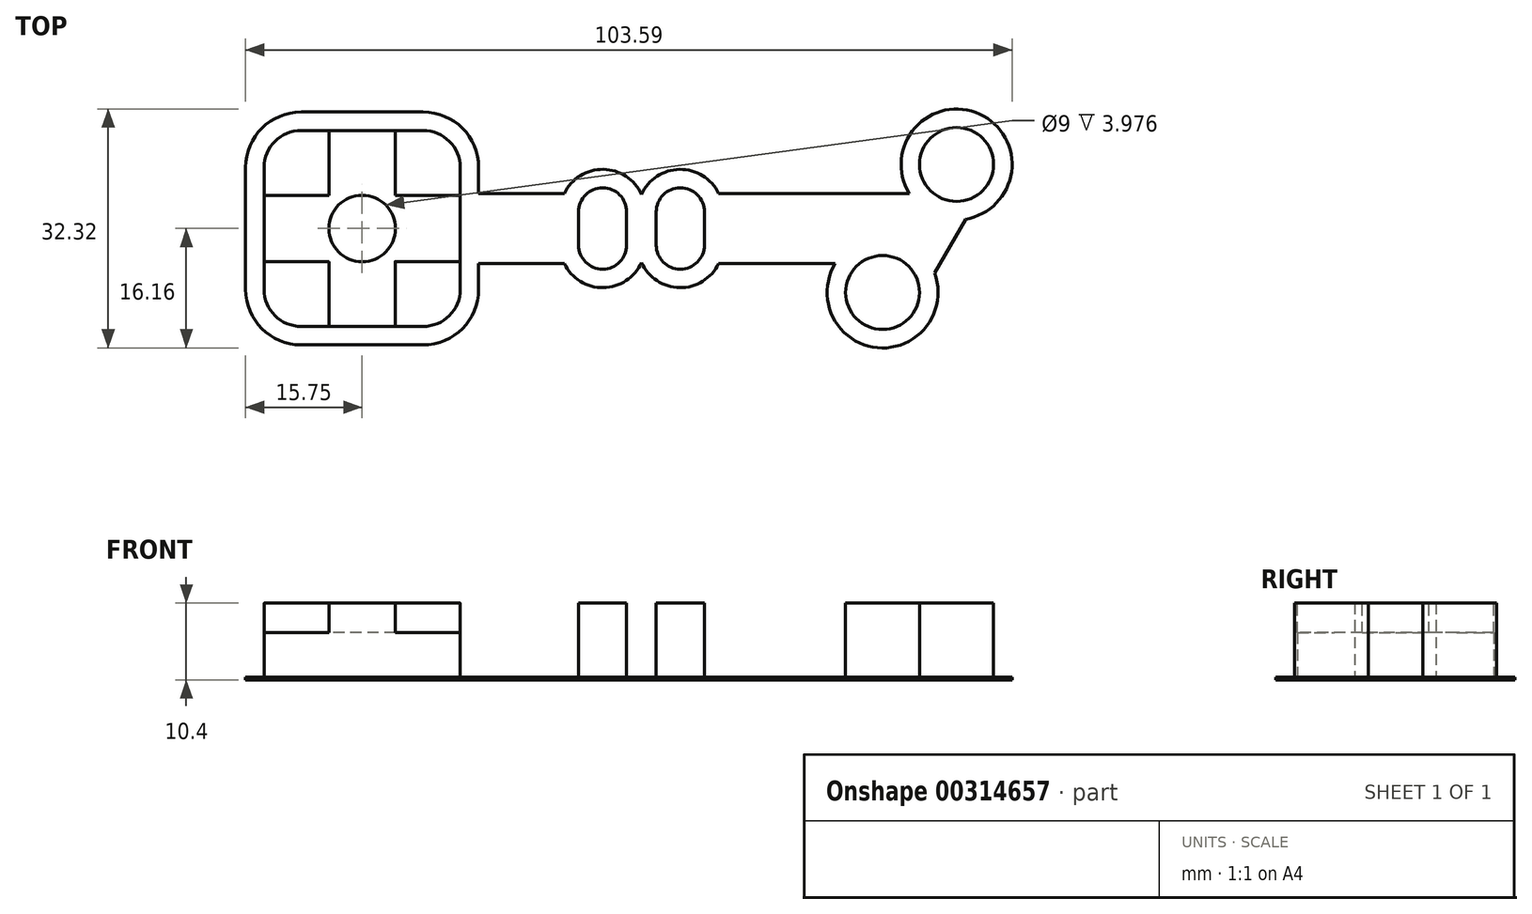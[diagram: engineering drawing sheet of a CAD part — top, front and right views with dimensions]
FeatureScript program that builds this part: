
annotation { "Feature Type Name" : "Feature", "Feature Type Description" : "" }
export const myFeature = defineFeature(function(context is Context, id is Id, definition is map)
    precondition{}
    {
        {
            var Q0;
            Q0=qCreatedBy(makeId("Top.planeOp"),FACE);
            var sketch = newSketch(context, id + "F0", { "sketchPlane" : qUnion([Q0])});
            skLineSegment(sketch, "E0.bottom", {"start": v(-8.25, 13.25) * mm, "end": v(8.25, 13.25) * mm});
            skLineSegment(sketch, "E0.top", {"start": v(-8.25, -13.25) * mm, "end": v(8.25, -13.25) * mm});
            skLineSegment(sketch, "E0.left", {"start": v(-13.25, 8.25) * mm, "end": v(-13.25, -8.25) * mm});
            skLineSegment(sketch, "E0.right", {"start": v(13.25, 8.25) * mm, "end": v(13.25, 2.25) * mm});
            skPoint(sketch, "E0.middle", {"position": v(0, 0) * mm});
            skPoint(sketch, "E1.visualSharp", {"position": v(-13.25, 13.25) * mm});
            skArc(sketch, "E1.filletArc", {"start": v(-8.25, 13.25) * mm, "mid": v(-11.79, 11.79) * mm, "end": v(-13.25, 8.25) * mm});
            skPoint(sketch, "E2.visualSharp", {"position": v(13.25, 13.25) * mm});
            skArc(sketch, "E2.filletArc", {"start": v(13.25, 8.25) * mm, "mid": v(11.79, 11.79) * mm, "end": v(8.25, 13.25) * mm});
            skPoint(sketch, "E3.visualSharp", {"position": v(13.25, -13.25) * mm});
            skArc(sketch, "E3.filletArc", {"start": v(8.25, -13.25) * mm, "mid": v(11.79, -11.79) * mm, "end": v(13.25, -8.25) * mm});
            skPoint(sketch, "E4.visualSharp", {"position": v(-13.25, -13.25) * mm});
            skArc(sketch, "E4.filletArc", {"start": v(-13.25, -8.25) * mm, "mid": v(-11.79, -11.79) * mm, "end": v(-8.25, -13.25) * mm});
            skCircle(sketch, "E5", {"center": v(0, 0) * mm, "radius": 4.5 * mm});
            skLineSegment(sketch, "E6", {"start": v(-93.44, 0) * mm, "end": v(130.36, 0) * mm, "construction": true});
            skPoint(sketch, "E6.startSnap0", {"position": v(-13.25, 0) * mm});
            skLineSegment(sketch, "E7", {"start": v(-4.5, 13.25) * mm, "end": v(-4.5, -13.25) * mm});
            skLineSegment(sketch, "E8", {"start": v(4.5, 13.25) * mm, "end": v(4.5, -13.25) * mm});
            skLineSegment(sketch, "E9", {"start": v(-13.25, -4.5) * mm, "end": v(13.25, -4.5) * mm});
            skLineSegment(sketch, "E10", {"start": v(-13.25, 4.5) * mm, "end": v(13.25, 4.5) * mm});
            skLineSegment(sketch, "E11", {"start": v(13.25, 2.25) * mm, "end": v(13.25, 2.25) * mm});
            skLineSegment(sketch, "E12.bottom", {"start": v(29.25, 2.25) * mm, "end": v(35.75, 2.25) * mm});
            skLineSegment(sketch, "E12.top", {"start": v(29.25, -2.25) * mm, "end": v(35.75, -2.25) * mm});
            skLineSegment(sketch, "E12.left", {"start": v(29.25, 2.25) * mm, "end": v(29.25, -2.25) * mm});
            skLineSegment(sketch, "E12.right", {"start": v(35.75, 2.25) * mm, "end": v(35.75, -2.25) * mm});
            skLineSegment(sketch, "E13", {"start": v(37.75, 15.2) * mm, "end": v(37.75, -16.91) * mm, "construction": true});
            skLineSegment(sketch, "E14.MirrorCS", {"start": v(13.25, -2.25) * mm, "end": v(29.25, -2.25) * mm});
            skLineSegment(sketch, "E15.MirrorCS", {"start": v(39.75, 2.25) * mm, "end": v(39.75, -2.25) * mm});
            skLineSegment(sketch, "E16.MirrorCS", {"start": v(46.25, -2.25) * mm, "end": v(39.75, -2.25) * mm});
            skLineSegment(sketch, "E17.MirrorCS", {"start": v(46.25, 2.25) * mm, "end": v(46.25, -2.25) * mm});
            skLineSegment(sketch, "E18.MirrorCS", {"start": v(46.25, 2.25) * mm, "end": v(39.75, 2.25) * mm});
            skLineSegment(sketch, "E19", {"start": v(35.75, 2.25) * mm, "end": v(39.75, 2.25) * mm});
            skLineSegment(sketch, "E20", {"start": v(39.75, -2.25) * mm, "end": v(35.75, -2.25) * mm});
            skArc(sketch, "E21", {"start": v(35.75, 2.25) * mm, "mid": v(32.5, 5.5) * mm, "end": v(29.25, 2.25) * mm});
            skArc(sketch, "E22", {"start": v(35.75, -2.25) * mm, "mid": v(32.5, -5.5) * mm, "end": v(29.25, -2.25) * mm});
            skArc(sketch, "E23.MirrorCS", {"start": v(39.75, 2.25) * mm, "mid": v(43, 5.5) * mm, "end": v(46.25, 2.25) * mm});
            skArc(sketch, "E24.MirrorCS", {"start": v(39.75, -2.25) * mm, "mid": v(43, -5.5) * mm, "end": v(46.25, -2.25) * mm});
            skLineSegment(sketch, "E25", {"start": v(46.25, 2.25) * mm, "end": v(74.04, 2.25) * mm});
            skLineSegment(sketch, "E26", {"start": v(80.34, 8.66) * mm, "end": v(70.34, -8.66) * mm, "construction": true});
            skPoint(sketch, "E27", {"position": v(75.34, 0) * mm});
            skLineSegment(sketch, "E28", {"start": v(76.16, 5.92) * mm, "end": v(74.04, 2.25) * mm});
            skPoint(sketch, "E29", {"position": v(73.39, 1.12) * mm});
            skLineSegment(sketch, "E30.MirrorCS", {"start": v(80.05, 3.67) * mm, "end": v(80.05, 3.67) * mm});
            skLineSegment(sketch, "E31.MirrorCS", {"start": v(46.25, -2.25) * mm, "end": v(71.44, -2.25) * mm});
            skPoint(sketch, "E32", {"position": v(72.74, 0) * mm});
            skPoint(sketch, "E33.orphan", {"position": v(72.75, -2.25) * mm});
            skPoint(sketch, "E34.orphan", {"position": v(72.75, 2.25) * mm});
            skLineSegment(sketch, "E35", {"start": v(13.25, 2.25) * mm, "end": v(29.25, 2.25) * mm});
            skLineSegment(sketch, "E36", {"start": v(13.25, -2.25) * mm, "end": v(13.25, -8.25) * mm});
            skLineSegment(sketch, "E37", {"start": v(13.25, 2.25) * mm, "end": v(13.25, -2.25) * mm});
            skLineSegment(sketch, "E38", {"start": v(71.44, -2.25) * mm, "end": v(70.62, -3.67) * mm});
            skLineSegment(sketch, "E39", {"start": v(74.04, 2.25) * mm, "end": v(71.44, -2.25) * mm});
            skArc(sketch, "E40", {"start": v(70.62, -3.67) * mm, "mid": v(67.84, -13) * mm, "end": v(74.52, -5.92) * mm});
            skArc(sketch, "E41", {"start": v(74.52, -5.92) * mm, "mid": v(72.84, -4.33) * mm, "end": v(70.62, -3.67) * mm});
            skLineSegment(sketch, "E42", {"start": v(80.05, 3.67) * mm, "end": v(74.52, -5.92) * mm});
            skArc(sketch, "E43", {"start": v(76.16, 5.92) * mm, "mid": v(77.84, 4.33) * mm, "end": v(80.05, 3.67) * mm});
            skArc(sketch, "E44", {"start": v(80.05, 3.67) * mm, "mid": v(82.84, 13) * mm, "end": v(76.16, 5.92) * mm});
            skLineSegment(sketch, "E45.0", {"start": v(-8.25, 15.75) * mm, "end": v(8.25, 15.75) * mm});
            skArc(sketch, "E45.1", {"start": v(15.75, 8.25) * mm, "mid": v(13.55, 13.55) * mm, "end": v(8.25, 15.75) * mm});
            skLineSegment(sketch, "E45.2", {"start": v(15.75, 8.25) * mm, "end": v(15.75, 4.75) * mm});
            skLineSegment(sketch, "E45.3", {"start": v(15.75, 4.75) * mm, "end": v(27.32, 4.75) * mm});
            skArc(sketch, "E45.4", {"start": v(37.75, 4.6) * mm, "mid": v(32.59, 8) * mm, "end": v(27.32, 4.75) * mm});
            skArc(sketch, "E45.5", {"start": v(-8.25, 15.75) * mm, "mid": v(-13.55, 13.55) * mm, "end": v(-15.75, 8.25) * mm});
            skArc(sketch, "E45.6", {"start": v(37.75, 4.6) * mm, "mid": v(42.91, 8) * mm, "end": v(48.18, 4.75) * mm});
            skLineSegment(sketch, "E45.7", {"start": v(48.18, 4.75) * mm, "end": v(73.94, 4.75) * mm});
            skArc(sketch, "E45.8", {"start": v(81.55, 1.26) * mm, "mid": v(83.46, 15.48) * mm, "end": v(73.94, 4.75) * mm});
            skLineSegment(sketch, "E45.9", {"start": v(81.55, 1.26) * mm, "end": v(77.35, -6) * mm});
            skArc(sketch, "E45.10", {"start": v(8.25, -15.75) * mm, "mid": v(13.55, -13.55) * mm, "end": v(15.75, -8.25) * mm});
            skLineSegment(sketch, "E45.11", {"start": v(-8.25, -15.75) * mm, "end": v(8.25, -15.75) * mm});
            skArc(sketch, "E45.12", {"start": v(-15.75, -8.25) * mm, "mid": v(-13.55, -13.55) * mm, "end": v(-8.25, -15.75) * mm});
            skLineSegment(sketch, "E45.13", {"start": v(-15.75, 8.25) * mm, "end": v(-15.75, -8.25) * mm});
            skLineSegment(sketch, "E45.14", {"start": v(15.75, -4.75) * mm, "end": v(15.75, -8.25) * mm});
            skLineSegment(sketch, "E45.15", {"start": v(15.75, -4.75) * mm, "end": v(27.32, -4.75) * mm});
            skArc(sketch, "E45.16", {"start": v(37.75, -4.6) * mm, "mid": v(32.59, -8) * mm, "end": v(27.32, -4.75) * mm});
            skArc(sketch, "E45.17", {"start": v(37.75, -4.6) * mm, "mid": v(42.91, -8) * mm, "end": v(48.18, -4.75) * mm});
            skLineSegment(sketch, "E45.18", {"start": v(48.18, -4.75) * mm, "end": v(63.94, -4.75) * mm});
            skArc(sketch, "E45.19", {"start": v(63.94, -4.75) * mm, "mid": v(69.64, -16.13) * mm, "end": v(77.35, -6) * mm});
            skSolve(sketch);
        }
        {
            var Q0;
            {var subQ15=sQuery(id+"F0.wireOp",EDGE,"E1.filletArc");Q0=makeQuery(id+"F0.imprint","IMPRINT",FACE,{"disambiguationData":[TD([[makeQuery(id+"F0.imprint","IMPRINT",EDGE,{"derivedFrom":subQ15}),-1.0]])]});}
            var Q1;
            {var subQ2=sQuery(id+"F0.wireOp",EDGE,"E7");var subQ5=sQuery(id+"F0.wireOp",EDGE,"E0.top");var subQ8=makeQuery(id+"F0.imprint","INTERSECT",VERTEX,{"derivedFrom":[subQ5,subQ2]});Q1=makeQuery(id+"F0.imprint","IMPRINT",FACE,{"disambiguationData":[TD([[makeQuery(id+"F0.imprint","IMPRINT",EDGE,{"disambiguationData":[TD([[subQ8,-1.0]])],"derivedFrom":subQ5}),1.0]])]});}
            var Q2;
            Q2=makeQuery(id+"F0.imprint","IMPRINT",FACE,{"disambiguationData":[TD([[makeQuery(id+"F0.imprint","IMPRINT",EDGE,{"derivedFrom":sQuery(id+"F0.wireOp",EDGE,"E28")}),1.0]])]});
            var Q3;
            Q3=makeQuery(id+"F0.imprint","IMPRINT",FACE,{"disambiguationData":[TD([[makeQuery(id+"F0.imprint","IMPRINT",EDGE,{"derivedFrom":sQuery(id+"F0.wireOp",EDGE,"E12.bottom")}),-1.0]])]});
            var Q4;
            Q4=makeQuery(id+"F0.imprint","IMPRINT",FACE,{"disambiguationData":[TD([[makeQuery(id+"F0.imprint","IMPRINT",EDGE,{"derivedFrom":sQuery(id+"F0.wireOp",EDGE,"E12.bottom")}),1.0]])]});
            var Q5;
            Q5=makeQuery(id+"F0.imprint","IMPRINT",FACE,{"disambiguationData":[TD([[makeQuery(id+"F0.imprint","IMPRINT",EDGE,{"derivedFrom":sQuery(id+"F0.wireOp",EDGE,"E17.MirrorCS")}),1.0]])]});
            var Q6;
            Q6=makeQuery(id+"F0.imprint","IMPRINT",FACE,{"disambiguationData":[TD([[makeQuery(id+"F0.imprint","IMPRINT",EDGE,{"derivedFrom":sQuery(id+"F0.wireOp",EDGE,"E12.top")}),-1.0]])]});
            var Q7;
            Q7=makeQuery(id+"F0.imprint","IMPRINT",FACE,{"disambiguationData":[TD([[makeQuery(id+"F0.imprint","IMPRINT",EDGE,{"derivedFrom":sQuery(id+"F0.wireOp",EDGE,"E12.right")}),1.0]])]});
            var Q8;
            {var subQ2=sQuery(id+"F0.wireOp",EDGE,"E9");var subQ6=sQuery(id+"F0.wireOp",EDGE,"E0.left");var subQ8=makeQuery(id+"F0.imprint","INTERSECT",VERTEX,{"derivedFrom":[subQ6,subQ2]});Q8=makeQuery(id+"F0.imprint","IMPRINT",FACE,{"disambiguationData":[TD([[makeQuery(id+"F0.imprint","IMPRINT",EDGE,{"disambiguationData":[TD([[subQ8,1.0]])],"derivedFrom":subQ6}),1.0]])]});}
            var Q9;
            Q9=makeQuery(id+"F0.imprint","IMPRINT",FACE,{"disambiguationData":[TD([[makeQuery(id+"F0.imprint","IMPRINT",EDGE,{"derivedFrom":sQuery(id+"F0.wireOp",EDGE,"E18.MirrorCS")}),-1.0]])]});
            var Q10;
            {var subQ5=sQuery(id+"F0.wireOp",EDGE,"E4.filletArc");Q10=makeQuery(id+"F0.imprint","IMPRINT",FACE,{"disambiguationData":[TD([[makeQuery(id+"F0.imprint","IMPRINT",EDGE,{"derivedFrom":subQ5}),1.0]])]});}
            var Q11;
            {var subQ5=sQuery(id+"F0.wireOp",EDGE,"E3.filletArc");Q11=makeQuery(id+"F0.imprint","IMPRINT",FACE,{"disambiguationData":[TD([[makeQuery(id+"F0.imprint","IMPRINT",EDGE,{"derivedFrom":subQ5}),1.0]])]});}
            var Q12;
            Q12=makeQuery(id+"F0.imprint","IMPRINT",FACE,{"disambiguationData":[TD([[makeQuery(id+"F0.imprint","IMPRINT",EDGE,{"derivedFrom":sQuery(id+"F0.wireOp",EDGE,"E16.MirrorCS")}),1.0]])]});
            var Q13;
            Q13=makeQuery(id+"F0.imprint","IMPRINT",FACE,{"disambiguationData":[TD([[makeQuery(id+"F0.imprint","IMPRINT",EDGE,{"derivedFrom":sQuery(id+"F0.wireOp",EDGE,"E40")}),1.0]])]});
            var Q14;
            Q14=makeQuery(id+"F0.imprint","IMPRINT",FACE,{"disambiguationData":[TD([[makeQuery(id+"F0.imprint","IMPRINT",EDGE,{"derivedFrom":sQuery(id+"F0.wireOp",EDGE,"E43")}),1.0]])]});
            var Q15;
            {var subQ8=sQuery(id+"F0.wireOp",EDGE,"E37");Q15=makeQuery(id+"F0.imprint","IMPRINT",FACE,{"disambiguationData":[TD([[makeQuery(id+"F0.imprint","IMPRINT",EDGE,{"derivedFrom":subQ8}),-1.0]])]});}
            var Q16;
            {var subQ5=sQuery(id+"F0.wireOp",EDGE,"E1.filletArc");Q16=makeQuery(id+"F0.imprint","IMPRINT",FACE,{"disambiguationData":[TD([[makeQuery(id+"F0.imprint","IMPRINT",EDGE,{"derivedFrom":subQ5}),1.0]])]});}
            var Q17;
            {var subQ2=sQuery(id+"F0.wireOp",EDGE,"E7");var subQ5=sQuery(id+"F0.wireOp",EDGE,"E0.bottom");var subQ8=makeQuery(id+"F0.imprint","INTERSECT",VERTEX,{"derivedFrom":[subQ5,subQ2]});Q17=makeQuery(id+"F0.imprint","IMPRINT",FACE,{"disambiguationData":[TD([[makeQuery(id+"F0.imprint","IMPRINT",EDGE,{"disambiguationData":[TD([[subQ8,-1.0]])],"derivedFrom":subQ5}),-1.0]])]});}
            var Q18;
            {var subQ5=sQuery(id+"F0.wireOp",EDGE,"E2.filletArc");Q18=makeQuery(id+"F0.imprint","IMPRINT",FACE,{"disambiguationData":[TD([[makeQuery(id+"F0.imprint","IMPRINT",EDGE,{"derivedFrom":subQ5}),1.0]])]});}
            var Q19;
            Q19=makeQuery(id+"F0.imprint","IMPRINT",FACE,{"disambiguationData":[TD([[makeQuery(id+"F0.imprint","IMPRINT",EDGE,{"derivedFrom":sQuery(id+"F0.wireOp",EDGE,"E12.left")}),-1.0]])]});
            var Q20;
            Q20=makeQuery(id+"F0.imprint","IMPRINT",FACE,{"disambiguationData":[TD([[makeQuery(id+"F0.imprint","IMPRINT",EDGE,{"derivedFrom":sQuery(id+"F0.wireOp",EDGE,"E15.MirrorCS")}),1.0]])]});
            var Q21;
            {var subQ0=sQuery(id+"F0.wireOp",EDGE,"E5");var subQ1=makeQuery(id+"F0.imprint","INTERSECT",VERTEX,{"derivedFrom":[subQ0,sQuery(id+"F0.wireOp",EDGE,"E10")]});Q21=makeQuery(id+"F0.imprint","IMPRINT",FACE,{"disambiguationData":[TD([[makeQuery(id+"F0.imprint","IMPRINT",EDGE,{"disambiguationData":[TD([[subQ1,1.0]])],"derivedFrom":subQ0}),1.0]])]});}
            var Q22;
            {var subQ0=sQuery(id+"F0.wireOp",EDGE,"E10");var subQ1=sQuery(id+"F0.wireOp",EDGE,"E5");var subQ2=makeQuery(id+"F0.imprint","INTERSECT",VERTEX,{"derivedFrom":[subQ1,subQ0]});Q22=makeQuery(id+"F0.imprint","IMPRINT",FACE,{"disambiguationData":[TD([[makeQuery(id+"F0.imprint","IMPRINT",EDGE,{"disambiguationData":[TD([[subQ2,1.0]])],"derivedFrom":subQ1}),-1.0]])]});}
            var Q23;
            {var subQ0=sQuery(id+"F0.wireOp",EDGE,"E8");var subQ1=sQuery(id+"F0.wireOp",EDGE,"E5");var subQ2=makeQuery(id+"F0.imprint","INTERSECT",VERTEX,{"derivedFrom":[subQ1,subQ0]});Q23=makeQuery(id+"F0.imprint","IMPRINT",FACE,{"disambiguationData":[TD([[makeQuery(id+"F0.imprint","IMPRINT",EDGE,{"disambiguationData":[TD([[subQ2,1.0]])],"derivedFrom":subQ1}),-1.0]])]});}
            var Q24;
            {var subQ0=sQuery(id+"F0.wireOp",EDGE,"E7");var subQ1=sQuery(id+"F0.wireOp",EDGE,"E5");var subQ2=makeQuery(id+"F0.imprint","INTERSECT",VERTEX,{"derivedFrom":[subQ1,subQ0]});Q24=makeQuery(id+"F0.imprint","IMPRINT",FACE,{"disambiguationData":[TD([[makeQuery(id+"F0.imprint","IMPRINT",EDGE,{"disambiguationData":[TD([[subQ2,-1.0]])],"derivedFrom":subQ1}),-1.0]])]});}
            var Q25;
            {var subQ0=sQuery(id+"F0.wireOp",EDGE,"E10");var subQ1=sQuery(id+"F0.wireOp",EDGE,"E5");var subQ2=makeQuery(id+"F0.imprint","INTERSECT",VERTEX,{"derivedFrom":[subQ1,subQ0]});Q25=makeQuery(id+"F0.imprint","IMPRINT",FACE,{"disambiguationData":[TD([[makeQuery(id+"F0.imprint","IMPRINT",EDGE,{"disambiguationData":[TD([[subQ2,-1.0]])],"derivedFrom":subQ1}),-1.0]])]});}
            extrude(context, id + "F1", {"entities" : qUnion([Q0, Q1, Q2, Q3, Q4, Q5, Q6, Q7, Q8, Q9, Q10, Q11, Q12, Q13, Q14, Q15, Q16, Q17, Q18, Q19, Q20, Q21, Q22, Q23, Q24, Q25]), "depth" : 0.4 * mm});
        }
        {
            var Q0;
            Q0=makeQuery(id+"F1.opExtrude","CAP_FACE",FACE,{"disambiguationData":[OSD([sQuery(id+"F0.wireOp",EDGE,"E45.0"),sQuery(id+"F0.wireOp",EDGE,"E45.1"),sQuery(id+"F0.wireOp",EDGE,"E45.2"),sQuery(id+"F0.wireOp",EDGE,"E45.3"),sQuery(id+"F0.wireOp",EDGE,"E45.4"),sQuery(id+"F0.wireOp",EDGE,"E45.5"),sQuery(id+"F0.wireOp",EDGE,"E45.6"),sQuery(id+"F0.wireOp",EDGE,"E45.7"),sQuery(id+"F0.wireOp",EDGE,"E45.8"),sQuery(id+"F0.wireOp",EDGE,"E45.9"),sQuery(id+"F0.wireOp",EDGE,"E45.10"),sQuery(id+"F0.wireOp",EDGE,"E45.11"),sQuery(id+"F0.wireOp",EDGE,"E45.12"),sQuery(id+"F0.wireOp",EDGE,"E45.13"),sQuery(id+"F0.wireOp",EDGE,"E45.14"),sQuery(id+"F0.wireOp",EDGE,"E45.15"),sQuery(id+"F0.wireOp",EDGE,"E45.16"),sQuery(id+"F0.wireOp",EDGE,"E45.17"),sQuery(id+"F0.wireOp",EDGE,"E45.18"),sQuery(id+"F0.wireOp",EDGE,"E45.19")])],"isStart":false});
            var sketch = newSketch(context, id + "F2", { "sketchPlane" : qUnion([Q0])});
            skLineSegment(sketch, "E46.0", {"start": v(-8.25, 13.25) * mm, "end": v(8.25, 13.25) * mm});
            skLineSegment(sketch, "E46.1", {"start": v(-8.25, -13.25) * mm, "end": v(8.25, -13.25) * mm});
            skLineSegment(sketch, "E46.2", {"start": v(-13.25, 8.25) * mm, "end": v(-13.25, -8.25) * mm});
            skLineSegment(sketch, "E46.3", {"start": v(13.25, 8.25) * mm, "end": v(13.25, 2.25) * mm});
            skPoint(sketch, "E46.4", {"position": v(0, 0) * mm});
            skPoint(sketch, "E46.5", {"position": v(-13.25, 13.25) * mm});
            skArc(sketch, "E46.6", {"start": v(-8.25, 13.25) * mm, "mid": v(-11.79, 11.79) * mm, "end": v(-13.25, 8.25) * mm});
            skPoint(sketch, "E46.7", {"position": v(13.25, 13.25) * mm});
            skArc(sketch, "E46.8", {"start": v(13.25, 8.25) * mm, "mid": v(11.79, 11.79) * mm, "end": v(8.25, 13.25) * mm});
            skPoint(sketch, "E46.9", {"position": v(13.25, -13.25) * mm});
            skArc(sketch, "E46.10", {"start": v(8.25, -13.25) * mm, "mid": v(11.79, -11.79) * mm, "end": v(13.25, -8.25) * mm});
            skPoint(sketch, "E46.11", {"position": v(-13.25, -13.25) * mm});
            skArc(sketch, "E46.12", {"start": v(-13.25, -8.25) * mm, "mid": v(-11.79, -11.79) * mm, "end": v(-8.25, -13.25) * mm});
            skCircle(sketch, "E46.13", {"center": v(0, 0) * mm, "radius": 4.5 * mm});
            skPoint(sketch, "E46.15", {"position": v(-13.25, 0) * mm});
            skLineSegment(sketch, "E46.16", {"start": v(-4.5, 13.25) * mm, "end": v(-4.5, -13.25) * mm});
            skLineSegment(sketch, "E46.17", {"start": v(4.5, 13.25) * mm, "end": v(4.5, -13.25) * mm});
            skLineSegment(sketch, "E46.18", {"start": v(-13.25, -4.5) * mm, "end": v(13.25, -4.5) * mm});
            skLineSegment(sketch, "E46.19", {"start": v(-13.25, 4.5) * mm, "end": v(13.25, 4.5) * mm});
            skPoint(sketch, "E46.20", {"position": v(13.25, 2.25) * mm});
            skLineSegment(sketch, "E46.21", {"start": v(29.25, 2.25) * mm, "end": v(35.75, 2.25) * mm});
            skLineSegment(sketch, "E46.22", {"start": v(29.25, -2.25) * mm, "end": v(35.75, -2.25) * mm});
            skLineSegment(sketch, "E46.23", {"start": v(29.25, 2.25) * mm, "end": v(29.25, -2.25) * mm});
            skLineSegment(sketch, "E46.24", {"start": v(35.75, 2.25) * mm, "end": v(35.75, -2.25) * mm});
            skLineSegment(sketch, "E46.26", {"start": v(13.25, -2.25) * mm, "end": v(29.25, -2.25) * mm});
            skLineSegment(sketch, "E46.27", {"start": v(39.75, 2.25) * mm, "end": v(39.75, -2.25) * mm});
            skLineSegment(sketch, "E46.28", {"start": v(46.25, -2.25) * mm, "end": v(39.75, -2.25) * mm});
            skLineSegment(sketch, "E46.29", {"start": v(46.25, 2.25) * mm, "end": v(46.25, -2.25) * mm});
            skLineSegment(sketch, "E46.30", {"start": v(46.25, 2.25) * mm, "end": v(39.75, 2.25) * mm});
            skLineSegment(sketch, "E46.31", {"start": v(35.75, 2.25) * mm, "end": v(39.75, 2.25) * mm});
            skLineSegment(sketch, "E46.32", {"start": v(39.75, -2.25) * mm, "end": v(35.75, -2.25) * mm});
            skArc(sketch, "E46.33", {"start": v(35.75, 2.25) * mm, "mid": v(32.5, 5.5) * mm, "end": v(29.25, 2.25) * mm});
            skArc(sketch, "E46.34", {"start": v(35.75, -2.25) * mm, "mid": v(32.5, -5.5) * mm, "end": v(29.25, -2.25) * mm});
            skArc(sketch, "E46.35", {"start": v(39.75, 2.25) * mm, "mid": v(43, 5.5) * mm, "end": v(46.25, 2.25) * mm});
            skArc(sketch, "E46.36", {"start": v(35.75, 2.25) * mm, "mid": v(32.5, 5.5) * mm, "end": v(29.25, 2.25) * mm});
            skArc(sketch, "E46.37", {"start": v(39.75, -2.25) * mm, "mid": v(43, -5.5) * mm, "end": v(46.25, -2.25) * mm});
            skLineSegment(sketch, "E46.38", {"start": v(46.25, 2.25) * mm, "end": v(74.04, 2.25) * mm});
            skLineSegment(sketch, "E46.39", {"start": v(80.34, 8.66) * mm, "end": v(70.34, -8.66) * mm});
            skPoint(sketch, "E46.40", {"position": v(75.34, 0) * mm});
            skLineSegment(sketch, "E46.41", {"start": v(76.16, 5.92) * mm, "end": v(74.04, 2.25) * mm});
            skPoint(sketch, "E46.42", {"position": v(73.39, 1.12) * mm});
            skPoint(sketch, "E46.43", {"position": v(80.05, 3.67) * mm});
            skLineSegment(sketch, "E46.44", {"start": v(46.25, -2.25) * mm, "end": v(71.44, -2.25) * mm});
            skPoint(sketch, "E46.45", {"position": v(72.74, 0) * mm});
            skPoint(sketch, "E46.46", {"position": v(72.75, -2.25) * mm});
            skPoint(sketch, "E46.47", {"position": v(72.75, 2.25) * mm});
            skLineSegment(sketch, "E46.48", {"start": v(13.25, 2.25) * mm, "end": v(29.25, 2.25) * mm});
            skLineSegment(sketch, "E46.49", {"start": v(13.25, -2.25) * mm, "end": v(13.25, -8.25) * mm});
            skLineSegment(sketch, "E46.50", {"start": v(13.25, 2.25) * mm, "end": v(13.25, -2.25) * mm});
            skLineSegment(sketch, "E46.51", {"start": v(71.44, -2.25) * mm, "end": v(70.62, -3.67) * mm});
            skLineSegment(sketch, "E46.52", {"start": v(74.04, 2.25) * mm, "end": v(71.44, -2.25) * mm});
            skArc(sketch, "E46.53", {"start": v(70.62, -3.67) * mm, "mid": v(67.84, -13) * mm, "end": v(74.52, -5.92) * mm});
            skArc(sketch, "E46.54", {"start": v(74.52, -5.92) * mm, "mid": v(72.84, -4.33) * mm, "end": v(70.62, -3.67) * mm});
            skLineSegment(sketch, "E46.55", {"start": v(80.05, 3.67) * mm, "end": v(74.52, -5.92) * mm});
            skArc(sketch, "E46.56", {"start": v(76.16, 5.92) * mm, "mid": v(77.84, 4.33) * mm, "end": v(80.05, 3.67) * mm});
            skArc(sketch, "E46.57", {"start": v(80.05, 3.67) * mm, "mid": v(82.84, 13) * mm, "end": v(76.16, 5.92) * mm});
            skLineSegment(sketch, "E46.58", {"start": v(-8.25, 15.75) * mm, "end": v(8.25, 15.75) * mm});
            skArc(sketch, "E46.59", {"start": v(15.75, 8.25) * mm, "mid": v(13.55, 13.55) * mm, "end": v(8.25, 15.75) * mm});
            skLineSegment(sketch, "E46.60", {"start": v(15.75, 8.25) * mm, "end": v(15.75, 4.75) * mm});
            skLineSegment(sketch, "E46.61", {"start": v(15.75, 4.75) * mm, "end": v(27.32, 4.75) * mm});
            skArc(sketch, "E46.62", {"start": v(37.75, 4.6) * mm, "mid": v(32.59, 8) * mm, "end": v(27.32, 4.75) * mm});
            skArc(sketch, "E46.63", {"start": v(-8.25, 15.75) * mm, "mid": v(-13.55, 13.55) * mm, "end": v(-15.75, 8.25) * mm});
            skArc(sketch, "E46.64", {"start": v(37.75, 4.6) * mm, "mid": v(42.91, 8) * mm, "end": v(48.18, 4.75) * mm});
            skLineSegment(sketch, "E46.65", {"start": v(48.18, 4.75) * mm, "end": v(73.94, 4.75) * mm});
            skArc(sketch, "E46.66", {"start": v(81.55, 1.26) * mm, "mid": v(83.46, 15.48) * mm, "end": v(73.94, 4.75) * mm});
            skLineSegment(sketch, "E46.67", {"start": v(81.55, 1.26) * mm, "end": v(77.35, -6) * mm});
            skArc(sketch, "E46.68", {"start": v(8.25, -15.75) * mm, "mid": v(13.55, -13.55) * mm, "end": v(15.75, -8.25) * mm});
            skLineSegment(sketch, "E46.69", {"start": v(-8.25, -15.75) * mm, "end": v(8.25, -15.75) * mm});
            skArc(sketch, "E46.70", {"start": v(-15.75, -8.25) * mm, "mid": v(-13.55, -13.55) * mm, "end": v(-8.25, -15.75) * mm});
            skLineSegment(sketch, "E46.71", {"start": v(-15.75, 8.25) * mm, "end": v(-15.75, -8.25) * mm});
            skLineSegment(sketch, "E46.72", {"start": v(15.75, -4.75) * mm, "end": v(15.75, -8.25) * mm});
            skLineSegment(sketch, "E46.73", {"start": v(15.75, -4.75) * mm, "end": v(27.32, -4.75) * mm});
            skArc(sketch, "E46.74", {"start": v(37.75, -4.6) * mm, "mid": v(32.59, -8) * mm, "end": v(27.32, -4.75) * mm});
            skArc(sketch, "E46.75", {"start": v(37.75, -4.6) * mm, "mid": v(42.91, -8) * mm, "end": v(48.18, -4.75) * mm});
            skLineSegment(sketch, "E46.76", {"start": v(48.18, -4.75) * mm, "end": v(63.94, -4.75) * mm});
            skArc(sketch, "E46.77", {"start": v(63.94, -4.75) * mm, "mid": v(69.64, -16.13) * mm, "end": v(77.35, -6) * mm});
            skSolve(sketch);
        }
        {
            var Q0;
            {var subQ2=sQuery(id+"F2.wireOp",EDGE,"E46.16");var subQ5=sQuery(id+"F2.wireOp",EDGE,"E46.0");var subQ8=makeQuery(id+"F2.imprint","INTERSECT",VERTEX,{"derivedFrom":[subQ5,subQ2]});Q0=makeQuery(id+"F2.imprint","IMPRINT",FACE,{"disambiguationData":[TD([[makeQuery(id+"F2.imprint","IMPRINT",EDGE,{"disambiguationData":[TD([[subQ8,-1.0]])],"derivedFrom":subQ5}),-1.0]])]});}
            var Q1;
            {var subQ2=sQuery(id+"F2.wireOp",EDGE,"E46.18");var subQ6=sQuery(id+"F2.wireOp",EDGE,"E46.2");var subQ8=makeQuery(id+"F2.imprint","INTERSECT",VERTEX,{"derivedFrom":[subQ6,subQ2]});Q1=makeQuery(id+"F2.imprint","IMPRINT",FACE,{"disambiguationData":[TD([[makeQuery(id+"F2.imprint","IMPRINT",EDGE,{"disambiguationData":[TD([[subQ8,1.0]])],"derivedFrom":subQ6}),1.0]])]});}
            var Q2;
            {var subQ4=sQuery(id+"F2.wireOp",EDGE,"E46.50");Q2=makeQuery(id+"F2.imprint","IMPRINT",FACE,{"disambiguationData":[TD([[makeQuery(id+"F2.imprint","IMPRINT",EDGE,{"derivedFrom":subQ4}),-1.0]])]});}
            var Q3;
            {var subQ2=sQuery(id+"F2.wireOp",EDGE,"E46.16");var subQ5=sQuery(id+"F2.wireOp",EDGE,"E46.1");var subQ8=makeQuery(id+"F2.imprint","INTERSECT",VERTEX,{"derivedFrom":[subQ5,subQ2]});Q3=makeQuery(id+"F2.imprint","IMPRINT",FACE,{"disambiguationData":[TD([[makeQuery(id+"F2.imprint","IMPRINT",EDGE,{"disambiguationData":[TD([[subQ8,-1.0]])],"derivedFrom":subQ5}),1.0]])]});}
            var Q4;
            {var subQ0=sQuery(id+"F2.wireOp",EDGE,"E46.17");var subQ1=sQuery(id+"F2.wireOp",EDGE,"E46.13");var subQ2=makeQuery(id+"F2.imprint","INTERSECT",VERTEX,{"derivedFrom":[subQ1,subQ0]});Q4=makeQuery(id+"F2.imprint","IMPRINT",FACE,{"disambiguationData":[TD([[makeQuery(id+"F2.imprint","IMPRINT",EDGE,{"disambiguationData":[TD([[subQ2,1.0]])],"derivedFrom":subQ1}),-1.0]])]});}
            var Q5;
            {var subQ0=sQuery(id+"F2.wireOp",EDGE,"E46.16");var subQ1=sQuery(id+"F2.wireOp",EDGE,"E46.13");var subQ2=makeQuery(id+"F2.imprint","INTERSECT",VERTEX,{"derivedFrom":[subQ1,subQ0]});Q5=makeQuery(id+"F2.imprint","IMPRINT",FACE,{"disambiguationData":[TD([[makeQuery(id+"F2.imprint","IMPRINT",EDGE,{"disambiguationData":[TD([[subQ2,-1.0]])],"derivedFrom":subQ1}),-1.0]])]});}
            var Q6;
            {var subQ0=sQuery(id+"F2.wireOp",EDGE,"E46.19");var subQ1=sQuery(id+"F2.wireOp",EDGE,"E46.13");var subQ2=makeQuery(id+"F2.imprint","INTERSECT",VERTEX,{"derivedFrom":[subQ1,subQ0]});Q6=makeQuery(id+"F2.imprint","IMPRINT",FACE,{"disambiguationData":[TD([[makeQuery(id+"F2.imprint","IMPRINT",EDGE,{"disambiguationData":[TD([[subQ2,-1.0]])],"derivedFrom":subQ1}),-1.0]])]});}
            var Q7;
            {var subQ0=sQuery(id+"F2.wireOp",EDGE,"E46.19");var subQ1=sQuery(id+"F2.wireOp",EDGE,"E46.13");var subQ2=makeQuery(id+"F2.imprint","INTERSECT",VERTEX,{"derivedFrom":[subQ1,subQ0]});Q7=makeQuery(id+"F2.imprint","IMPRINT",FACE,{"disambiguationData":[TD([[makeQuery(id+"F2.imprint","IMPRINT",EDGE,{"disambiguationData":[TD([[subQ2,1.0]])],"derivedFrom":subQ1}),-1.0]])]});}
            var Q8;
            Q8=makeQuery(id+"F2.imprint","IMPRINT",FACE,{"disambiguationData":[TD([[makeQuery(id+"F2.imprint","IMPRINT",EDGE,{"derivedFrom":sQuery(id+"F2.wireOp",EDGE,"E46.21")}),-1.0]])]});
            var Q9;
            Q9=makeQuery(id+"F2.imprint","IMPRINT",FACE,{"disambiguationData":[TD([[makeQuery(id+"F2.imprint","IMPRINT",EDGE,{"derivedFrom":sQuery(id+"F2.wireOp",EDGE,"E46.21")}),1.0]])]});
            var Q10;
            Q10=makeQuery(id+"F2.imprint","IMPRINT",FACE,{"disambiguationData":[TD([[makeQuery(id+"F2.imprint","IMPRINT",EDGE,{"derivedFrom":sQuery(id+"F2.wireOp",EDGE,"E46.22")}),-1.0]])]});
            var Q11;
            Q11=makeQuery(id+"F2.imprint","IMPRINT",FACE,{"disambiguationData":[TD([[makeQuery(id+"F2.imprint","IMPRINT",EDGE,{"derivedFrom":sQuery(id+"F2.wireOp",EDGE,"E46.30")}),-1.0]])]});
            var Q12;
            Q12=makeQuery(id+"F2.imprint","IMPRINT",FACE,{"disambiguationData":[TD([[makeQuery(id+"F2.imprint","IMPRINT",EDGE,{"derivedFrom":sQuery(id+"F2.wireOp",EDGE,"E46.27")}),1.0]])]});
            var Q13;
            Q13=makeQuery(id+"F2.imprint","IMPRINT",FACE,{"disambiguationData":[TD([[makeQuery(id+"F2.imprint","IMPRINT",EDGE,{"derivedFrom":sQuery(id+"F2.wireOp",EDGE,"E46.28")}),1.0]])]});
            var Q14;
            {var subQ0=sQuery(id+"F2.wireOp",EDGE,"E46.57");Q14=makeQuery(id+"F2.imprint","IMPRINT",FACE,{"disambiguationData":[TD([[makeQuery(id+"F2.imprint","IMPRINT",EDGE,{"derivedFrom":subQ0}),1.0]])]});}
            var Q15;
            {var subQ0=sQuery(id+"F2.wireOp",EDGE,"E46.53");Q15=makeQuery(id+"F2.imprint","IMPRINT",FACE,{"disambiguationData":[TD([[makeQuery(id+"F2.imprint","IMPRINT",EDGE,{"derivedFrom":subQ0}),1.0]])]});}
            var Q16;
            {var subQ5=sQuery(id+"F2.wireOp",EDGE,"E46.8");Q16=makeQuery(id+"F2.imprint","IMPRINT",FACE,{"disambiguationData":[TD([[makeQuery(id+"F2.imprint","IMPRINT",EDGE,{"derivedFrom":subQ5}),1.0]])]});}
            var Q17;
            {var subQ5=sQuery(id+"F2.wireOp",EDGE,"E46.6");Q17=makeQuery(id+"F2.imprint","IMPRINT",FACE,{"disambiguationData":[TD([[makeQuery(id+"F2.imprint","IMPRINT",EDGE,{"derivedFrom":subQ5}),1.0]])]});}
            var Q18;
            {var subQ5=sQuery(id+"F2.wireOp",EDGE,"E46.12");Q18=makeQuery(id+"F2.imprint","IMPRINT",FACE,{"disambiguationData":[TD([[makeQuery(id+"F2.imprint","IMPRINT",EDGE,{"derivedFrom":subQ5}),1.0]])]});}
            var Q19;
            {var subQ0=sQuery(id+"F2.wireOp",EDGE,"E46.13");var subQ1=makeQuery(id+"F2.imprint","INTERSECT",VERTEX,{"derivedFrom":[subQ0,sQuery(id+"F2.wireOp",EDGE,"E46.19")]});Q19=makeQuery(id+"F2.imprint","IMPRINT",FACE,{"disambiguationData":[TD([[makeQuery(id+"F2.imprint","IMPRINT",EDGE,{"disambiguationData":[TD([[subQ1,1.0]])],"derivedFrom":subQ0}),1.0]])]});}
            var Q20;
            {var subQ5=sQuery(id+"F2.wireOp",EDGE,"E46.10");Q20=makeQuery(id+"F2.imprint","IMPRINT",FACE,{"disambiguationData":[TD([[makeQuery(id+"F2.imprint","IMPRINT",EDGE,{"derivedFrom":subQ5}),1.0]])]});}
            extrude(context, id + "F3", {"entities" : qUnion([Q0, Q1, Q2, Q3, Q4, Q5, Q6, Q7, Q8, Q9, Q10, Q11, Q12, Q13, Q14, Q15, Q16, Q17, Q18, Q19, Q20]), "operationType" : NewBodyOperationType.ADD, "depth" : 10 * mm});
        }
        {
            var Q0;
            Q0=makeQuery(id+"F3.opExtrude","CAP_FACE",FACE,{"disambiguationData":[OSD([sQuery(id+"F2.wireOp",EDGE,"E46.0"),sQuery(id+"F2.wireOp",EDGE,"E46.1"),sQuery(id+"F2.wireOp",EDGE,"E46.2"),sQuery(id+"F2.wireOp",EDGE,"E46.3"),sQuery(id+"F2.wireOp",EDGE,"E46.6"),sQuery(id+"F2.wireOp",EDGE,"E46.8"),sQuery(id+"F2.wireOp",EDGE,"E46.10"),sQuery(id+"F2.wireOp",EDGE,"E46.12"),sQuery(id+"F2.wireOp",EDGE,"E46.49"),sQuery(id+"F2.wireOp",EDGE,"E46.50")])],"isStart":false});
            var sketch = newSketch(context, id + "F4", { "sketchPlane" : qUnion([Q0])});
            skLineSegment(sketch, "E47.0", {"start": v(-8.25, 13.25) * mm, "end": v(8.25, 13.25) * mm});
            skLineSegment(sketch, "E47.1", {"start": v(-8.25, -13.25) * mm, "end": v(8.25, -13.25) * mm});
            skLineSegment(sketch, "E47.2", {"start": v(-13.25, 8.25) * mm, "end": v(-13.25, -8.25) * mm});
            skLineSegment(sketch, "E47.3", {"start": v(13.25, 8.25) * mm, "end": v(13.25, 2.25) * mm});
            skPoint(sketch, "E47.4", {"position": v(0, 0) * mm});
            skPoint(sketch, "E47.5", {"position": v(-13.25, 13.25) * mm});
            skArc(sketch, "E47.6", {"start": v(-8.25, 13.25) * mm, "mid": v(-11.79, 11.79) * mm, "end": v(-13.25, 8.25) * mm});
            skPoint(sketch, "E47.7", {"position": v(13.25, 13.25) * mm});
            skArc(sketch, "E47.8", {"start": v(13.25, 8.25) * mm, "mid": v(11.79, 11.79) * mm, "end": v(8.25, 13.25) * mm});
            skPoint(sketch, "E47.9", {"position": v(13.25, -13.25) * mm});
            skArc(sketch, "E47.10", {"start": v(8.25, -13.25) * mm, "mid": v(11.79, -11.79) * mm, "end": v(13.25, -8.25) * mm});
            skPoint(sketch, "E47.11", {"position": v(-13.25, -13.25) * mm});
            skArc(sketch, "E47.12", {"start": v(-13.25, -8.25) * mm, "mid": v(-11.79, -11.79) * mm, "end": v(-8.25, -13.25) * mm});
            skCircle(sketch, "E47.13", {"center": v(0, 0) * mm, "radius": 4.5 * mm});
            skPoint(sketch, "E47.15", {"position": v(-13.25, 0) * mm});
            skLineSegment(sketch, "E47.16", {"start": v(-4.5, 13.25) * mm, "end": v(-4.5, -13.25) * mm});
            skLineSegment(sketch, "E47.17", {"start": v(4.5, 13.25) * mm, "end": v(4.5, -13.25) * mm});
            skLineSegment(sketch, "E47.18", {"start": v(-13.25, -4.5) * mm, "end": v(13.25, -4.5) * mm});
            skLineSegment(sketch, "E47.19", {"start": v(-13.25, 4.5) * mm, "end": v(13.25, 4.5) * mm});
            skPoint(sketch, "E47.20", {"position": v(13.25, 2.25) * mm});
            skLineSegment(sketch, "E47.21", {"start": v(29.25, 2.25) * mm, "end": v(35.75, 2.25) * mm});
            skLineSegment(sketch, "E47.22", {"start": v(29.25, -2.25) * mm, "end": v(35.75, -2.25) * mm});
            skLineSegment(sketch, "E47.23", {"start": v(29.25, 2.25) * mm, "end": v(29.25, -2.25) * mm});
            skLineSegment(sketch, "E47.24", {"start": v(35.75, 2.25) * mm, "end": v(35.75, -2.25) * mm});
            skLineSegment(sketch, "E47.26", {"start": v(13.25, -2.25) * mm, "end": v(29.25, -2.25) * mm});
            skLineSegment(sketch, "E47.27", {"start": v(39.75, 2.25) * mm, "end": v(39.75, -2.25) * mm});
            skLineSegment(sketch, "E47.28", {"start": v(46.25, -2.25) * mm, "end": v(39.75, -2.25) * mm});
            skLineSegment(sketch, "E47.29", {"start": v(46.25, 2.25) * mm, "end": v(46.25, -2.25) * mm});
            skLineSegment(sketch, "E47.30", {"start": v(46.25, 2.25) * mm, "end": v(39.75, 2.25) * mm});
            skLineSegment(sketch, "E47.31", {"start": v(35.75, 2.25) * mm, "end": v(39.75, 2.25) * mm});
            skLineSegment(sketch, "E47.32", {"start": v(39.75, -2.25) * mm, "end": v(35.75, -2.25) * mm});
            skArc(sketch, "E47.33", {"start": v(35.75, 2.25) * mm, "mid": v(32.5, 5.5) * mm, "end": v(29.25, 2.25) * mm});
            skArc(sketch, "E47.34", {"start": v(35.75, -2.25) * mm, "mid": v(32.5, -5.5) * mm, "end": v(29.25, -2.25) * mm});
            skArc(sketch, "E47.35", {"start": v(39.75, 2.25) * mm, "mid": v(43, 5.5) * mm, "end": v(46.25, 2.25) * mm});
            skArc(sketch, "E47.36", {"start": v(35.75, 2.25) * mm, "mid": v(32.5, 5.5) * mm, "end": v(29.25, 2.25) * mm});
            skArc(sketch, "E47.37", {"start": v(39.75, -2.25) * mm, "mid": v(43, -5.5) * mm, "end": v(46.25, -2.25) * mm});
            skLineSegment(sketch, "E47.38", {"start": v(46.25, 2.25) * mm, "end": v(74.04, 2.25) * mm});
            skLineSegment(sketch, "E47.39", {"start": v(80.34, 8.66) * mm, "end": v(70.34, -8.66) * mm});
            skPoint(sketch, "E47.40", {"position": v(75.34, 0) * mm});
            skLineSegment(sketch, "E47.41", {"start": v(76.16, 5.92) * mm, "end": v(74.04, 2.25) * mm});
            skPoint(sketch, "E47.42", {"position": v(73.39, 1.12) * mm});
            skPoint(sketch, "E47.43", {"position": v(80.05, 3.67) * mm});
            skLineSegment(sketch, "E47.44", {"start": v(46.25, -2.25) * mm, "end": v(71.44, -2.25) * mm});
            skPoint(sketch, "E47.45", {"position": v(72.74, 0) * mm});
            skPoint(sketch, "E47.46", {"position": v(72.75, -2.25) * mm});
            skPoint(sketch, "E47.47", {"position": v(72.75, 2.25) * mm});
            skLineSegment(sketch, "E47.48", {"start": v(13.25, 2.25) * mm, "end": v(29.25, 2.25) * mm});
            skLineSegment(sketch, "E47.49", {"start": v(13.25, -2.25) * mm, "end": v(13.25, -8.25) * mm});
            skLineSegment(sketch, "E47.50", {"start": v(13.25, 2.25) * mm, "end": v(13.25, -2.25) * mm});
            skLineSegment(sketch, "E47.51", {"start": v(71.44, -2.25) * mm, "end": v(70.62, -3.67) * mm});
            skLineSegment(sketch, "E47.52", {"start": v(74.04, 2.25) * mm, "end": v(71.44, -2.25) * mm});
            skArc(sketch, "E47.53", {"start": v(70.62, -3.67) * mm, "mid": v(67.84, -13) * mm, "end": v(74.52, -5.92) * mm});
            skArc(sketch, "E47.54", {"start": v(74.52, -5.92) * mm, "mid": v(72.84, -4.33) * mm, "end": v(70.62, -3.67) * mm});
            skLineSegment(sketch, "E47.55", {"start": v(80.05, 3.67) * mm, "end": v(74.52, -5.92) * mm});
            skArc(sketch, "E47.56", {"start": v(76.16, 5.92) * mm, "mid": v(77.84, 4.33) * mm, "end": v(80.05, 3.67) * mm});
            skArc(sketch, "E47.57", {"start": v(80.05, 3.67) * mm, "mid": v(82.84, 13) * mm, "end": v(76.16, 5.92) * mm});
            skLineSegment(sketch, "E47.58", {"start": v(-8.25, 15.75) * mm, "end": v(8.25, 15.75) * mm});
            skArc(sketch, "E47.59", {"start": v(15.75, 8.25) * mm, "mid": v(13.55, 13.55) * mm, "end": v(8.25, 15.75) * mm});
            skLineSegment(sketch, "E47.60", {"start": v(15.75, 8.25) * mm, "end": v(15.75, 4.75) * mm});
            skLineSegment(sketch, "E47.61", {"start": v(15.75, 4.75) * mm, "end": v(27.32, 4.75) * mm});
            skArc(sketch, "E47.62", {"start": v(37.75, 4.6) * mm, "mid": v(32.59, 8) * mm, "end": v(27.32, 4.75) * mm});
            skArc(sketch, "E47.63", {"start": v(-8.25, 15.75) * mm, "mid": v(-13.55, 13.55) * mm, "end": v(-15.75, 8.25) * mm});
            skArc(sketch, "E47.64", {"start": v(37.75, 4.6) * mm, "mid": v(42.91, 8) * mm, "end": v(48.18, 4.75) * mm});
            skLineSegment(sketch, "E47.65", {"start": v(48.18, 4.75) * mm, "end": v(73.94, 4.75) * mm});
            skArc(sketch, "E47.66", {"start": v(81.55, 1.26) * mm, "mid": v(83.46, 15.48) * mm, "end": v(73.94, 4.75) * mm});
            skLineSegment(sketch, "E47.67", {"start": v(81.55, 1.26) * mm, "end": v(77.35, -6) * mm});
            skArc(sketch, "E47.68", {"start": v(8.25, -15.75) * mm, "mid": v(13.55, -13.55) * mm, "end": v(15.75, -8.25) * mm});
            skLineSegment(sketch, "E47.69", {"start": v(-8.25, -15.75) * mm, "end": v(8.25, -15.75) * mm});
            skArc(sketch, "E47.70", {"start": v(-15.75, -8.25) * mm, "mid": v(-13.55, -13.55) * mm, "end": v(-8.25, -15.75) * mm});
            skLineSegment(sketch, "E47.71", {"start": v(-15.75, 8.25) * mm, "end": v(-15.75, -8.25) * mm});
            skLineSegment(sketch, "E47.72", {"start": v(15.75, -4.75) * mm, "end": v(15.75, -8.25) * mm});
            skLineSegment(sketch, "E47.73", {"start": v(15.75, -4.75) * mm, "end": v(27.32, -4.75) * mm});
            skArc(sketch, "E47.74", {"start": v(37.75, -4.6) * mm, "mid": v(32.59, -8) * mm, "end": v(27.32, -4.75) * mm});
            skArc(sketch, "E47.75", {"start": v(37.75, -4.6) * mm, "mid": v(42.91, -8) * mm, "end": v(48.18, -4.75) * mm});
            skLineSegment(sketch, "E47.76", {"start": v(48.18, -4.75) * mm, "end": v(63.94, -4.75) * mm});
            skArc(sketch, "E47.77", {"start": v(63.94, -4.75) * mm, "mid": v(69.64, -16.13) * mm, "end": v(77.35, -6) * mm});
            skSolve(sketch);
        }
        {
            var Q0;
            {var subQ5=sQuery(id+"F4.wireOp",EDGE,"E47.8");Q0=makeQuery(id+"F4.imprint","IMPRINT",FACE,{"disambiguationData":[TD([[makeQuery(id+"F4.imprint","IMPRINT",EDGE,{"derivedFrom":subQ5}),1.0]])]});}
            var Q1;
            {var subQ5=sQuery(id+"F4.wireOp",EDGE,"E47.6");Q1=makeQuery(id+"F4.imprint","IMPRINT",FACE,{"disambiguationData":[TD([[makeQuery(id+"F4.imprint","IMPRINT",EDGE,{"derivedFrom":subQ5}),1.0]])]});}
            var Q2;
            {var subQ5=sQuery(id+"F4.wireOp",EDGE,"E47.12");Q2=makeQuery(id+"F4.imprint","IMPRINT",FACE,{"disambiguationData":[TD([[makeQuery(id+"F4.imprint","IMPRINT",EDGE,{"derivedFrom":subQ5}),1.0]])]});}
            var Q3;
            {var subQ5=sQuery(id+"F4.wireOp",EDGE,"E47.10");Q3=makeQuery(id+"F4.imprint","IMPRINT",FACE,{"disambiguationData":[TD([[makeQuery(id+"F4.imprint","IMPRINT",EDGE,{"derivedFrom":subQ5}),1.0]])]});}
            var Q4;
            {var subQ0=sQuery(id+"F4.wireOp",EDGE,"E47.13");var subQ1=makeQuery(id+"F4.imprint","INTERSECT",VERTEX,{"derivedFrom":[subQ0,sQuery(id+"F4.wireOp",EDGE,"E47.19")]});Q4=makeQuery(id+"F4.imprint","IMPRINT",FACE,{"disambiguationData":[TD([[makeQuery(id+"F4.imprint","IMPRINT",EDGE,{"disambiguationData":[TD([[subQ1,1.0]])],"derivedFrom":subQ0}),1.0]])]});}
            extrude(context, id + "F5", {"entities" : qUnion([Q0, Q1, Q2, Q3, Q4]), "operationType" : NewBodyOperationType.REMOVE, "oppositeDirection" : true, "depth" : 4 * mm});
        }
        {
            var Q0;
            Q0=makeQuery(id+"F3.opExtrude","CAP_FACE",FACE,{"disambiguationData":[OSD([sQuery(id+"F2.wireOp",EDGE,"E46.0"),sQuery(id+"F2.wireOp",EDGE,"E46.1"),sQuery(id+"F2.wireOp",EDGE,"E46.2"),sQuery(id+"F2.wireOp",EDGE,"E46.3"),sQuery(id+"F2.wireOp",EDGE,"E46.6"),sQuery(id+"F2.wireOp",EDGE,"E46.8"),sQuery(id+"F2.wireOp",EDGE,"E46.10"),sQuery(id+"F2.wireOp",EDGE,"E46.12"),sQuery(id+"F2.wireOp",EDGE,"E46.49"),sQuery(id+"F2.wireOp",EDGE,"E46.50")])],"isStart":false});
            fillet(context, id + "F6", {"entities" : qUnion([Q0]), "radius" : 0.02 * mm, "tangentPropagation" : true, "allowEdgeOverflow" : false});
        }
    });
